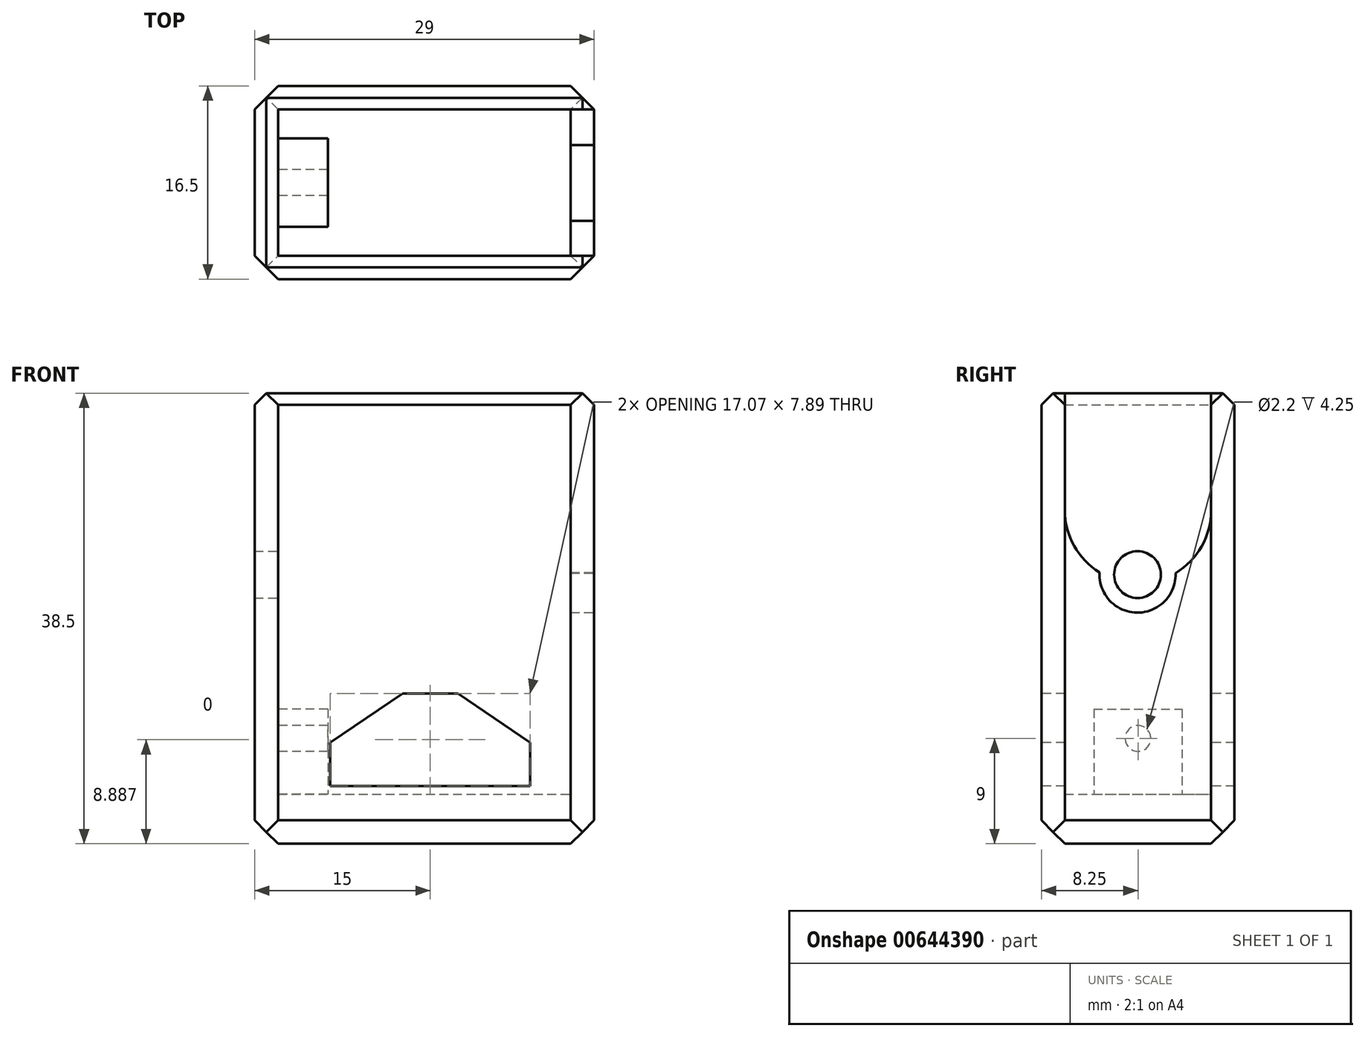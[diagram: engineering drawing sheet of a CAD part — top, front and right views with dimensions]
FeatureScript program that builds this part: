
annotation { "Feature Type Name" : "Feature", "Feature Type Description" : "" }
export const myFeature = defineFeature(function(context is Context, id is Id, definition is map)
    precondition{}
    {
        {
            var Q0;
            Q0=qCreatedBy(makeId("Top.planeOp"),FACE);
            var sketch = newSketch(context, id + "F0", { "sketchPlane" : qUnion([Q0])});
            skLineSegment(sketch, "E0.bottom", {"start": v(0, 0) * mm, "end": v(29, 0) * mm});
            skLineSegment(sketch, "E0.top", {"start": v(0, 16.5) * mm, "end": v(29, 16.5) * mm});
            skLineSegment(sketch, "E0.left", {"start": v(0, 0) * mm, "end": v(0, 16.5) * mm});
            skLineSegment(sketch, "E0.right", {"start": v(29, 0) * mm, "end": v(29, 16.5) * mm});
            skSolve(sketch);
        }
        {
            var Q0;
            Q0 = qSketchRegion(id + "F0", true);
            extrude(context, id + "F1", {"entities" : qUnion([Q0]), "depth" : 38.5 * mm, "offsetDistance" : 25 * mm});
        }
        {
            var Q0;
            Q0=makeQuery(id+"F1.opExtrude","CAP_FACE",FACE,{"disambiguationData":[OSD([sQuery(id+"F0.wireOp",EDGE,"E0.bottom"),sQuery(id+"F0.wireOp",EDGE,"E0.top"),sQuery(id+"F0.wireOp",EDGE,"E0.left"),sQuery(id+"F0.wireOp",EDGE,"E0.right")])],"isStart":false});
            shell(context, id + "F2", {"entities" : qUnion([Q0]), "thickness" : 2 * mm});
        }
        {
            var Q0;
            Q0=makeQuery(id+"F2.opShell","OFFSET_FACE",FACE,{"disambiguationData":[OSD([sQuery(id+"F0.wireOp",EDGE,"E0.bottom"),sQuery(id+"F0.wireOp",EDGE,"E0.top"),sQuery(id+"F0.wireOp",EDGE,"E0.left"),sQuery(id+"F0.wireOp",EDGE,"E0.right")])]});
            extrude(context, id + "F3", {"entities" : qUnion([Q0]), "operationType" : NewBodyOperationType.ADD, "depth" : 2.25 * mm, "offsetDistance" : 25 * mm});
        }
        {
            var Q0;
            Q0=makeQuery(id+"F1.opExtrude","SWEPT_EDGE",EDGE,{"disambiguationData":[OSD([sQuery(id+"F0.wireOp",EDGE,"E0.bottom"),sQuery(id+"F0.wireOp",EDGE,"E0.left")])]});
            var Q1;
            Q1=makeQuery(id+"F1.opExtrude","SWEPT_EDGE",EDGE,{"disambiguationData":[OSD([sQuery(id+"F0.wireOp",EDGE,"E0.top"),sQuery(id+"F0.wireOp",EDGE,"E0.left")])]});
            var Q2;
            Q2=makeQuery(id+"F1.opExtrude","SWEPT_EDGE",EDGE,{"disambiguationData":[OSD([sQuery(id+"F0.wireOp",EDGE,"E0.top"),sQuery(id+"F0.wireOp",EDGE,"E0.right")])]});
            var Q3;
            Q3=makeQuery(id+"F1.opExtrude","SWEPT_EDGE",EDGE,{"disambiguationData":[OSD([sQuery(id+"F0.wireOp",EDGE,"E0.bottom"),sQuery(id+"F0.wireOp",EDGE,"E0.right")])]});
            chamfer(context, id + "F4", {"entities" : qUnion([Q0, Q1, Q2, Q3]), "width" : 2 * mm, "tangentPropagation" : true});
        }
        {
            var Q0;
            Q0=makeQuery(id+"F1.opExtrude","CAP_EDGE",EDGE,{"disambiguationData":[OSD([sQuery(id+"F0.wireOp",EDGE,"E0.top")])],"isStart":true});
            var Q1;
            Q1=makeQuery(id+"F1.opExtrude","CAP_EDGE",EDGE,{"disambiguationData":[OSD([sQuery(id+"F0.wireOp",EDGE,"E0.right")])],"isStart":true});
            var Q2;
            Q2=makeQuery(id+"F1.opExtrude","CAP_EDGE",EDGE,{"disambiguationData":[OSD([sQuery(id+"F0.wireOp",EDGE,"E0.bottom")])],"isStart":true});
            var Q3;
            Q3=makeQuery(id+"F1.opExtrude","CAP_EDGE",EDGE,{"disambiguationData":[OSD([sQuery(id+"F0.wireOp",EDGE,"E0.left")])],"isStart":true});
            chamfer(context, id + "F5", {"entities" : qUnion([Q0, Q1, Q2, Q3]), "width" : 2 * mm, "tangentPropagation" : true});
        }
        {
            var Q0;
            Q0=makeQuery(id+"F1.opExtrude","CAP_EDGE",EDGE,{"disambiguationData":[OSD([sQuery(id+"F0.wireOp",EDGE,"E0.top")])],"isStart":false});
            var Q1;
            Q1=makeQuery(id+"F1.opExtrude","CAP_EDGE",EDGE,{"disambiguationData":[OSD([sQuery(id+"F0.wireOp",EDGE,"E0.left")])],"isStart":false});
            var Q2;
            Q2=makeQuery(id+"F1.opExtrude","CAP_EDGE",EDGE,{"disambiguationData":[OSD([sQuery(id+"F0.wireOp",EDGE,"E0.bottom")])],"isStart":false});
            var Q3;
            Q3=makeQuery(id+"F1.opExtrude","CAP_EDGE",EDGE,{"disambiguationData":[OSD([sQuery(id+"F0.wireOp",EDGE,"E0.right")])],"isStart":false});
            chamfer(context, id + "F6", {"entities" : qUnion([Q0, Q1, Q2, Q3]), "width" : 1 * mm, "tangentPropagation" : true});
        }
        {
            var Q0;
            Q0=makeQuery(id+"F1.opExtrude","SWEPT_FACE",FACE,{"disambiguationData":[OSD([sQuery(id+"F0.wireOp",EDGE,"E0.bottom")])]});
            var sketch = newSketch(context, id + "F7", { "sketchPlane" : qUnion([Q0])});
            skLineSegment(sketch, "E1", {"start": v(6.46, 4.94) * mm, "end": v(23.54, 4.94) * mm});
            skLineSegment(sketch, "E2", {"start": v(23.54, 4.94) * mm, "end": v(23.54, 8.66) * mm});
            skLineSegment(sketch, "E3", {"start": v(23.54, 8.66) * mm, "end": v(17.36, 12.83) * mm});
            skLineSegment(sketch, "E4", {"start": v(17.36, 12.83) * mm, "end": v(12.63, 12.83) * mm});
            skLineSegment(sketch, "E5", {"start": v(12.63, 12.83) * mm, "end": v(6.46, 8.66) * mm});
            skLineSegment(sketch, "E6", {"start": v(6.46, 8.66) * mm, "end": v(6.46, 4.94) * mm});
            skSolve(sketch);
        }
        {
            var Q0;
            Q0=makeQuery(id+"F7.imprint","IMPRINT",FACE,{"disambiguationData":[TD([[makeQuery(id+"F7.imprint","IMPRINT",EDGE,{"derivedFrom":sQuery(id+"F7.wireOp",EDGE,"E1")}),1.0]])]});
            extrude(context, id + "F8", {"entities" : qUnion([Q0]), "operationType" : NewBodyOperationType.REMOVE, "endBound" : BoundingType.THROUGH_ALL, "oppositeDirection" : true, "depth" : 25 * mm, "offsetDistance" : 25 * mm});
        }
        {
            var Q0;
            Q0=makeQuery(id+"F1.opExtrude","SWEPT_FACE",FACE,{"disambiguationData":[OSD([sQuery(id+"F0.wireOp",EDGE,"E0.right")])]});
            var sketch = newSketch(context, id + "F9", { "sketchPlane" : qUnion([Q0])});
            skCircle(sketch, "E7", {"center": v(8.25, 28.5) * mm, "radius": 6.25 * mm});
            skCircle(sketch, "E8", {"center": v(8.21, 23) * mm, "radius": 3.25 * mm});
            skLineSegment(sketch, "E9.bottom", {"start": v(2, 38.5) * mm, "end": v(14.5, 38.5) * mm});
            skLineSegment(sketch, "E9.top", {"start": v(2, 28.5) * mm, "end": v(14.5, 28.5) * mm});
            skLineSegment(sketch, "E9.left", {"start": v(2, 38.5) * mm, "end": v(2, 28.5) * mm});
            skLineSegment(sketch, "E9.right", {"start": v(14.5, 38.5) * mm, "end": v(14.5, 28.5) * mm});
            skSolve(sketch);
        }
        {
            var Q0;
            Q0 = qSketchRegion(id + "F9", true);
            extrude(context, id + "F10", {"entities" : qUnion([Q0]), "operationType" : NewBodyOperationType.REMOVE, "endBound" : BoundingType.UP_TO_NEXT, "oppositeDirection" : true, "depth" : 25 * mm, "offsetDistance" : 25 * mm});
        }
        {
            var Q0;
            Q0=makeQuery(id+"F2.opShell","OFFSET_FACE",FACE,{"disambiguationData":[OSD([sQuery(id+"F0.wireOp",EDGE,"E0.left")])]});
            var sketch = newSketch(context, id + "F11", { "sketchPlane" : qUnion([Q0])});
            skCircle(sketch, "E10", {"center": v(8.21, 23) * mm, "radius": 2 * mm});
            skSolve(sketch);
        }
        {
            var Q0;
            Q0 = qSketchRegion(id + "F11", true);
            extrude(context, id + "F12", {"entities" : qUnion([Q0]), "operationType" : NewBodyOperationType.REMOVE, "endBound" : BoundingType.THROUGH_ALL, "oppositeDirection" : true, "depth" : 25 * mm, "offsetDistance" : 25 * mm});
        }
        {
            var Q0;
            Q0=makeQuery(id+"F2.opShell","OFFSET_FACE",FACE,{"disambiguationData":[OSD([sQuery(id+"F0.wireOp",EDGE,"E0.left")])]});
            var sketch = newSketch(context, id + "F13", { "sketchPlane" : qUnion([Q0])});
            skLineSegment(sketch, "E11.bottom", {"start": v(4.48, 11.5) * mm, "end": v(12.02, 11.5) * mm});
            skLineSegment(sketch, "E11.top", {"start": v(4.48, 4.25) * mm, "end": v(12.02, 4.25) * mm});
            skLineSegment(sketch, "E11.left", {"start": v(4.48, 11.5) * mm, "end": v(4.48, 4.25) * mm});
            skLineSegment(sketch, "E11.right", {"start": v(12.02, 11.5) * mm, "end": v(12.02, 4.25) * mm});
            skCircle(sketch, "E12", {"center": v(8.25, 9) * mm, "radius": 1.1 * mm});
            skSolve(sketch);
        }
        {
            var Q0;
            Q0 = qSketchRegion(id + "F13", true);
            extrude(context, id + "F14", {"entities" : qUnion([Q0]), "operationType" : NewBodyOperationType.ADD, "depth" : 4.25 * mm, "offsetDistance" : 25 * mm});
        }
        {
            var Q0;
            Q0=makeQuery(id+"F1.opExtrude","SWEPT_FACE",FACE,{"disambiguationData":[OSD([sQuery(id+"F0.wireOp",EDGE,"E0.right")])]});
            var sketch = newSketch(context, id + "F15", { "sketchPlane" : qUnion([Q0])});
            skLineSegment(sketch, "E13.bottom", {"start": v(5.48, 10.8) * mm, "end": v(11.02, 10.8) * mm});
            skLineSegment(sketch, "E13.top", {"start": v(5.48, 5.27) * mm, "end": v(11.02, 5.27) * mm});
            skLineSegment(sketch, "E13.left", {"start": v(5.48, 10.8) * mm, "end": v(5.48, 5.27) * mm});
            skLineSegment(sketch, "E13.right", {"start": v(11.02, 10.8) * mm, "end": v(11.02, 5.27) * mm});
            skSolve(sketch);
        }
    });
